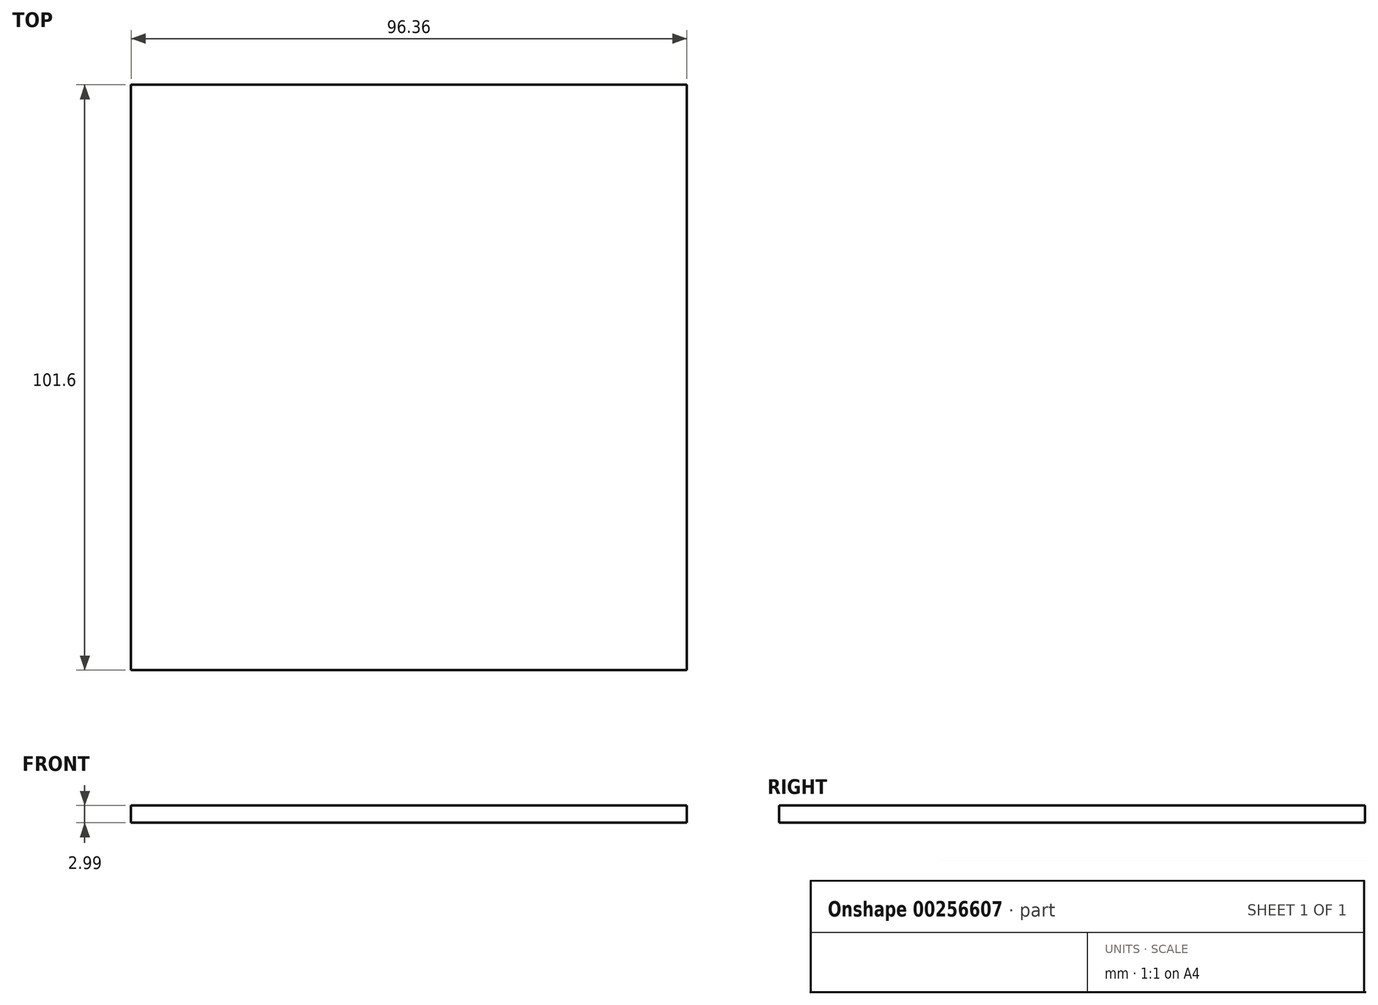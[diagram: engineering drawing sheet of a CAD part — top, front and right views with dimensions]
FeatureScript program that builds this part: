
annotation { "Feature Type Name" : "Feature", "Feature Type Description" : "" }
export const myFeature = defineFeature(function(context is Context, id is Id, definition is map)
    precondition{}
    {
        {
            var Q0;
            Q0=qCreatedBy(makeId("Front.planeOp"),FACE);
            var sketch = newSketch(context, id + "F0", { "sketchPlane" : qUnion([Q0])});
            skLineSegment(sketch, "E0.bottom", {"start": v(50.8, 26.56) * mm, "end": v(-50.8, 26.56) * mm});
            skLineSegment(sketch, "E0.top", {"start": v(50.8, 32.91) * mm, "end": v(-50.8, 32.91) * mm});
            skLineSegment(sketch, "E0.left", {"start": v(50.8, 26.56) * mm, "end": v(50.8, 32.91) * mm});
            skLineSegment(sketch, "E0.right", {"start": v(-50.8, 26.56) * mm, "end": v(-50.8, 32.91) * mm});
            skPoint(sketch, "E0.middle", {"position": v(0, 29.74) * mm});
            skLineSegment(sketch, "E1.bottom", {"start": v(48.18, 23.32) * mm, "end": v(-48.18, 23.32) * mm});
            skLineSegment(sketch, "E1.top", {"start": v(48.18, 26.31) * mm, "end": v(-48.18, 26.31) * mm});
            skLineSegment(sketch, "E1.left", {"start": v(48.18, 23.32) * mm, "end": v(48.18, 26.31) * mm});
            skLineSegment(sketch, "E1.right", {"start": v(-48.18, 23.32) * mm, "end": v(-48.18, 26.31) * mm});
            skPoint(sketch, "E1.middle", {"position": v(0, 24.82) * mm});
            skPoint(sketch, "E1.middle.positionSnap0", {"position": v(0, 26.56) * mm});
            skPoint(sketch, "E1.centerSnap0", {"position": v(0, 26.56) * mm});
            skLineSegment(sketch, "E2.bottom", {"start": v(-48.18, 23.32) * mm, "end": v(-43.1, 23.32) * mm});
            skLineSegment(sketch, "E2.top", {"start": v(-48.18, -16.05) * mm, "end": v(-43.1, -16.05) * mm});
            skLineSegment(sketch, "E2.left", {"start": v(-48.18, 23.32) * mm, "end": v(-48.18, -16.05) * mm});
            skLineSegment(sketch, "E2.right", {"start": v(-43.1, 23.32) * mm, "end": v(-43.1, -16.05) * mm});
            skLineSegment(sketch, "E3.bottom", {"start": v(48.18, 23.32) * mm, "end": v(43.1, 23.32) * mm});
            skLineSegment(sketch, "E3.top", {"start": v(48.18, -16.05) * mm, "end": v(43.1, -16.05) * mm});
            skLineSegment(sketch, "E3.left", {"start": v(48.18, 23.32) * mm, "end": v(48.18, -16.05) * mm});
            skLineSegment(sketch, "E3.right", {"start": v(43.1, 23.32) * mm, "end": v(43.1, -16.05) * mm});
            skSolve(sketch);
        }
        {
            var Q0;
            Q0=makeQuery(id+"F0.imprint","IMPRINT",FACE,{"disambiguationData":[TD([[makeQuery(id+"F0.imprint","IMPRINT",EDGE,{"derivedFrom":sQuery(id+"F0.wireOp",EDGE,"E1.bottom")}),-1.0]])]});
            extrude(context, id + "F1", {"entities" : qUnion([Q0]), "depth" : 101.6 * mm});
        }
    });
